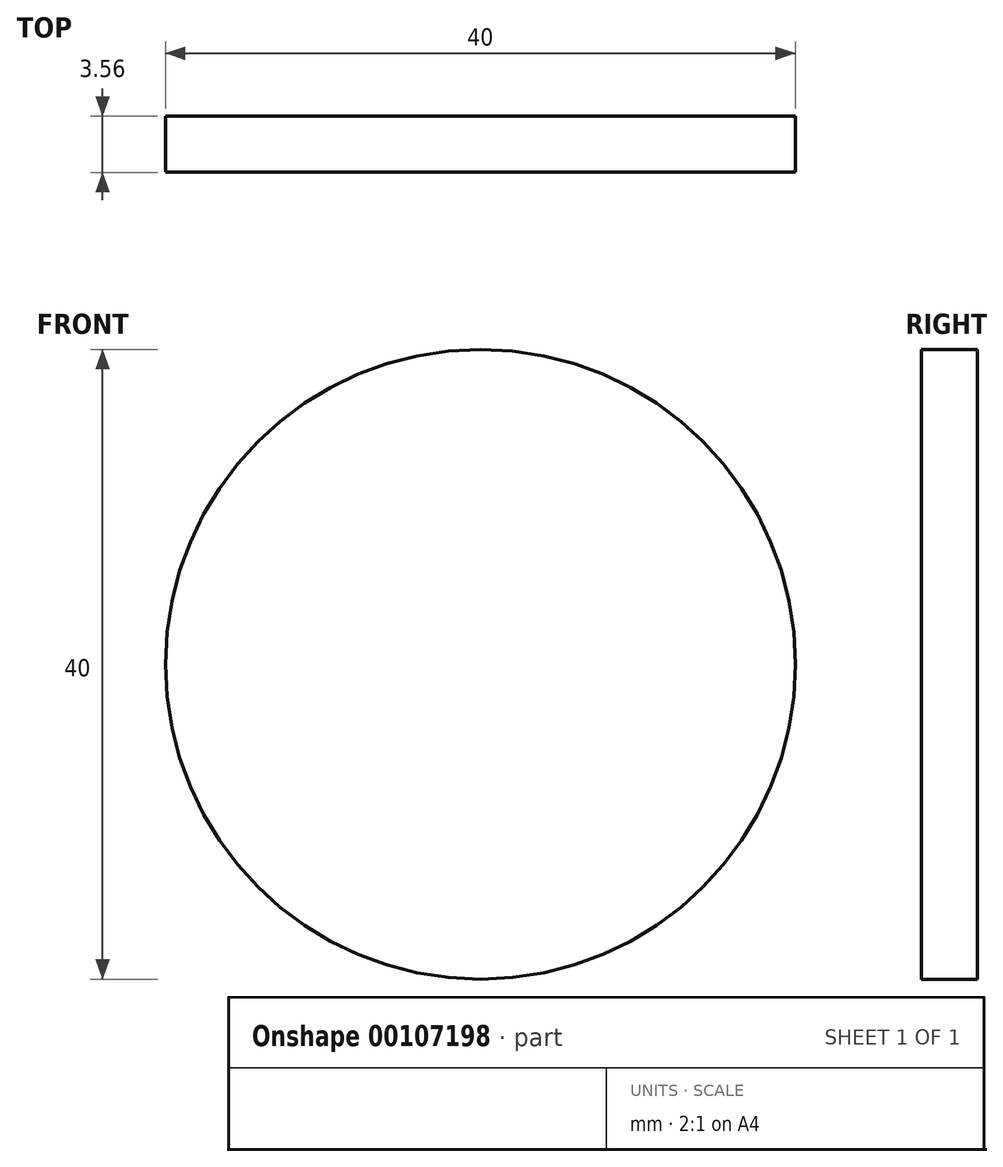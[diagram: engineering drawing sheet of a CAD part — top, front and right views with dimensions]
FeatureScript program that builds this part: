
annotation { "Feature Type Name" : "Feature", "Feature Type Description" : "" }
export const myFeature = defineFeature(function(context is Context, id is Id, definition is map)
    precondition{}
    {
        {
            var Q0;
            Q0=qCreatedBy(makeId("Front.planeOp"),FACE);
            var sketch = newSketch(context, id + "F0", { "sketchPlane" : qUnion([Q0])});
            skCircle(sketch, "E0", {"center": v(0, 0) * mm, "radius": 20 * mm});
            skSolve(sketch);
        }
        {
            var Q0;
            Q0=makeQuery(id+"F0.imprint","IMPRINT",FACE,{"disambiguationData":[TD([[makeQuery(id+"F0.imprint","IMPRINT",EDGE,{"derivedFrom":sQuery(id+"F0.wireOp",EDGE,"E0")}),1.0]])]});
            extrude(context, id + "F1", {"entities" : qUnion([Q0]), "depth" : 3.56 * mm});
        }
    });
